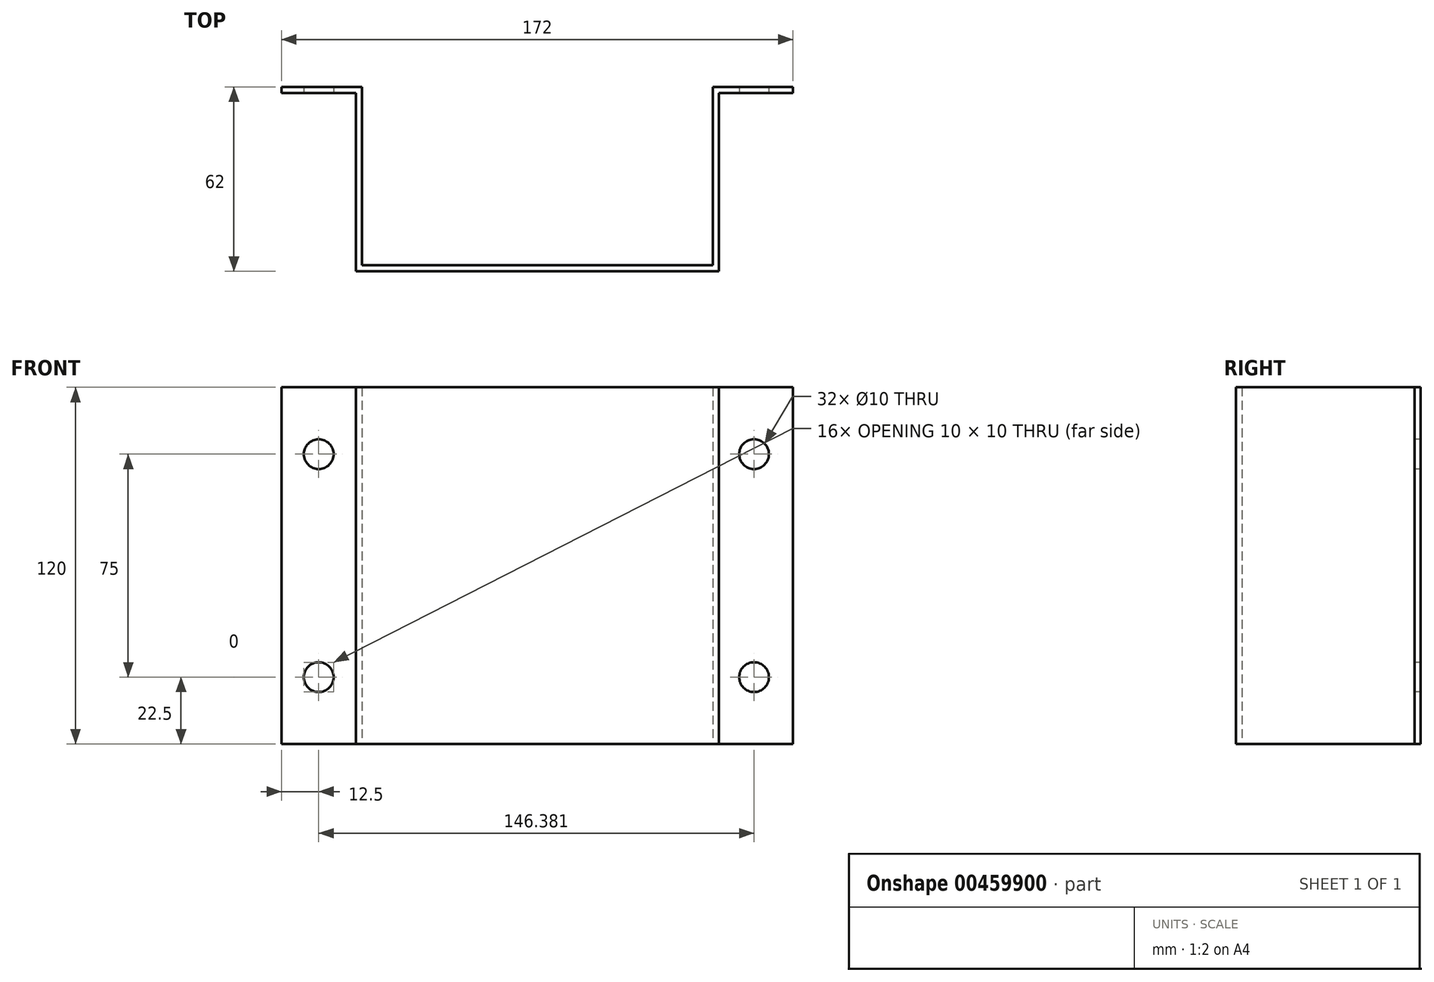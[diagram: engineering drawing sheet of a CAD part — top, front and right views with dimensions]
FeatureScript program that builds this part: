
annotation { "Feature Type Name" : "Feature", "Feature Type Description" : "" }
export const myFeature = defineFeature(function(context is Context, id is Id, definition is map)
    precondition{}
    {
        {
            var Q0;
            Q0=qCreatedBy(makeId("Top.planeOp"),FACE);
            var sketch = newSketch(context, id + "F0", { "sketchPlane" : qUnion([Q0])});
            skLineSegment(sketch, "E0", {"start": v(-86, 0) * mm, "end": v(-59, 0) * mm});
            skLineSegment(sketch, "E1", {"start": v(-59, 0) * mm, "end": v(-59, -60) * mm});
            skLineSegment(sketch, "E2", {"start": v(-59, -60) * mm, "end": v(59, -60) * mm});
            skLineSegment(sketch, "E3", {"start": v(59, -60) * mm, "end": v(59, 0) * mm});
            skLineSegment(sketch, "E4", {"start": v(59, 0) * mm, "end": v(86, 0) * mm});
            skLineSegment(sketch, "E5.0", {"start": v(61, -2) * mm, "end": v(86, -2) * mm});
            skLineSegment(sketch, "E5.1", {"start": v(-86, -2) * mm, "end": v(-61, -2) * mm});
            skLineSegment(sketch, "E5.2", {"start": v(-61, -2) * mm, "end": v(-61, -62) * mm});
            skLineSegment(sketch, "E5.3", {"start": v(-61, -62) * mm, "end": v(61, -62) * mm});
            skLineSegment(sketch, "E5.4", {"start": v(61, -62) * mm, "end": v(61, -2) * mm});
            skLineSegment(sketch, "E6", {"start": v(-86, -2) * mm, "end": v(-86, 0) * mm});
            skLineSegment(sketch, "E7", {"start": v(86, 0) * mm, "end": v(86, -2) * mm});
            skSolve(sketch);
        }
        {
            var Q0;
            Q0=makeQuery(id+"F0.imprint","IMPRINT",FACE,{"disambiguationData":[TD([[makeQuery(id+"F0.imprint","IMPRINT",EDGE,{"derivedFrom":sQuery(id+"F0.wireOp",EDGE,"E0")}),-1.0]])]});
            extrude(context, id + "F1", {"entities" : qUnion([Q0]), "depth" : 120 * mm});
        }
        {
            var Q0;
            Q0=makeQuery(id+"F1.opExtrude","SWEPT_FACE",FACE,{"disambiguationData":[OSD([sQuery(id+"F0.wireOp",EDGE,"E5.1")])]});
            var sketch = newSketch(context, id + "F2", { "sketchPlane" : qUnion([Q0])});
            skCircle(sketch, "E8", {"center": v(-73.5, 22.5) * mm, "radius": 5 * mm});
            skCircle(sketch, "E9", {"center": v(-73.5, 97.5) * mm, "radius": 5 * mm});
            skSolve(sketch);
        }
        {
            var Q0;
            Q0=makeQuery(id+"F2.imprint","IMPRINT",FACE,{"disambiguationData":[TD([[makeQuery(id+"F2.imprint","IMPRINT",EDGE,{"derivedFrom":sQuery(id+"F2.wireOp",EDGE,"E9")}),1.0]])]});
            var Q1;
            Q1=makeQuery(id+"F2.imprint","IMPRINT",FACE,{"disambiguationData":[TD([[makeQuery(id+"F2.imprint","IMPRINT",EDGE,{"derivedFrom":sQuery(id+"F2.wireOp",EDGE,"E8")}),1.0]])]});
            extrude(context, id + "F3", {"entities" : qUnion([Q0, Q1]), "operationType" : NewBodyOperationType.REMOVE, "oppositeDirection" : true, "depth" : 25 * mm});
        }
        {
            var Q0;
            Q0=makeQuery(id+"F1.opExtrude","SWEPT_FACE",FACE,{"disambiguationData":[OSD([sQuery(id+"F0.wireOp",EDGE,"E5.0")])]});
            var sketch = newSketch(context, id + "F4", { "sketchPlane" : qUnion([Q0])});
            skCircle(sketch, "E10", {"center": v(72.88, 97.5) * mm, "radius": 5 * mm});
            skCircle(sketch, "E11", {"center": v(72.88, 22.5) * mm, "radius": 5 * mm});
            skSolve(sketch);
        }
        {
            var Q0;
            Q0=makeQuery(id+"F4.imprint","IMPRINT",FACE,{"disambiguationData":[TD([[makeQuery(id+"F4.imprint","IMPRINT",EDGE,{"derivedFrom":sQuery(id+"F4.wireOp",EDGE,"E10")}),1.0]])]});
            var Q1;
            Q1=makeQuery(id+"F4.imprint","IMPRINT",FACE,{"disambiguationData":[TD([[makeQuery(id+"F4.imprint","IMPRINT",EDGE,{"derivedFrom":sQuery(id+"F4.wireOp",EDGE,"E11")}),1.0]])]});
            extrude(context, id + "F5", {"entities" : qUnion([Q0, Q1]), "operationType" : NewBodyOperationType.REMOVE, "oppositeDirection" : true, "depth" : 25 * mm});
        }
    });
